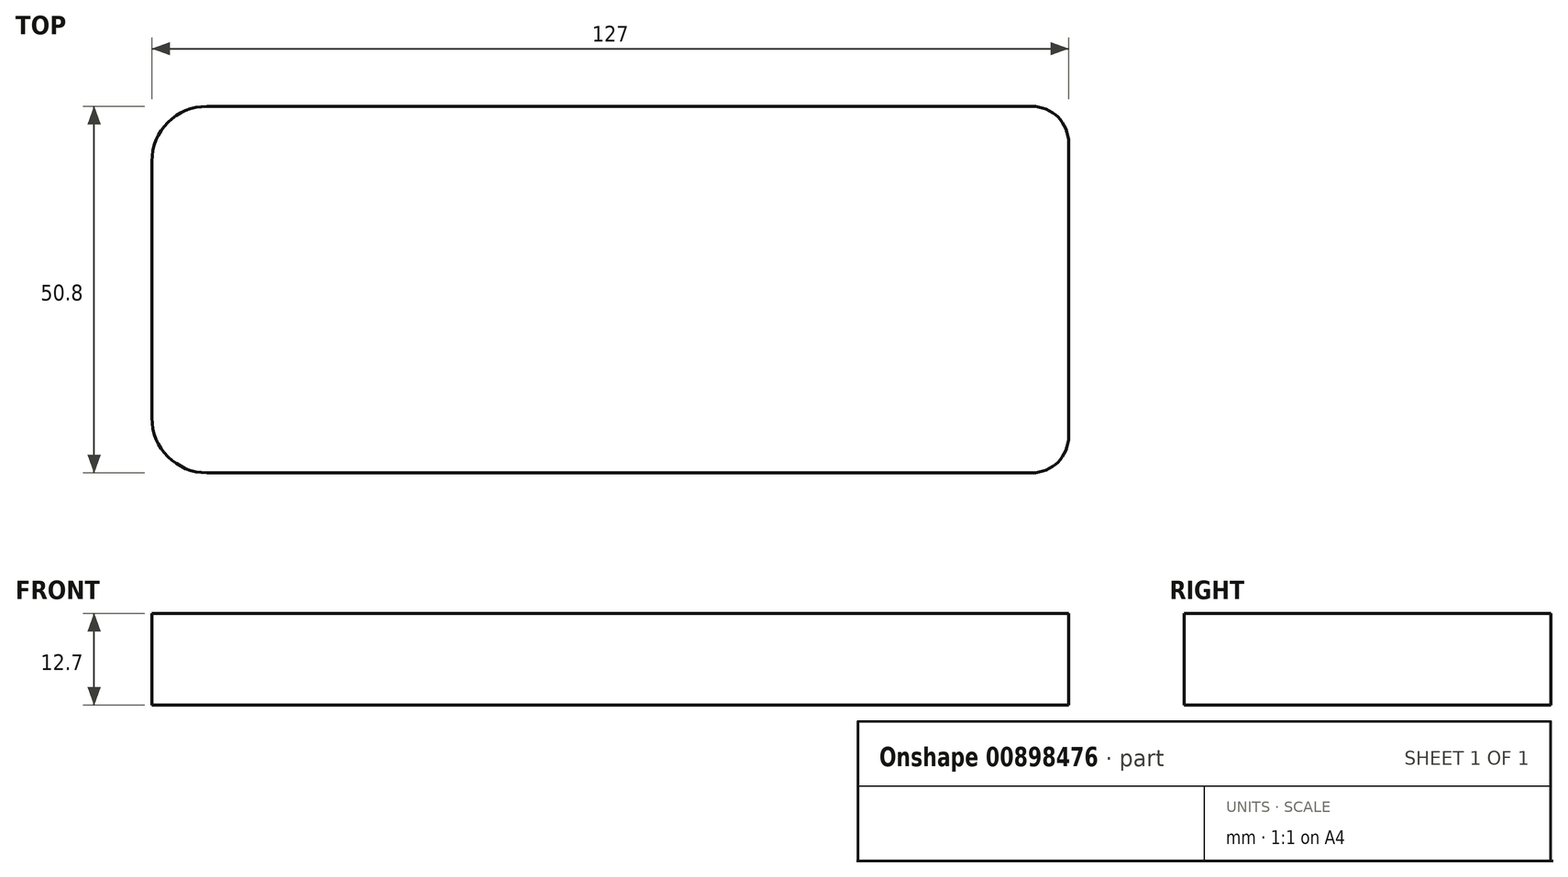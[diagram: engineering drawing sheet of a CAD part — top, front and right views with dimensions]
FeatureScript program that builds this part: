
annotation { "Feature Type Name" : "Feature", "Feature Type Description" : "" }
export const myFeature = defineFeature(function(context is Context, id is Id, definition is map)
    precondition{}
    {
        {
            var Q0;
            Q0=qCreatedBy(makeId("Top.planeOp"),FACE);
            var sketch = newSketch(context, id + "F0", { "sketchPlane" : qUnion([Q0])});
            skLineSegment(sketch, "E0", {"start": v(0, 0) * mm, "end": v(60.96, 0) * mm, "construction": true});
            skLineSegment(sketch, "E1", {"start": v(0, 0) * mm, "end": v(-66.04, 0) * mm, "construction": true});
            skPoint(sketch, "E2", {"position": v(30.48, 0) * mm});
            skLineSegment(sketch, "E3", {"start": v(30.48, 0) * mm, "end": v(30.48, -25.4) * mm, "construction": true});
            skLineSegment(sketch, "E4", {"start": v(30.48, 0) * mm, "end": v(30.48, 25.4) * mm, "construction": true});
            skLineSegment(sketch, "E5", {"start": v(30.48, 25.4) * mm, "end": v(50.8, 25.4) * mm});
            skLineSegment(sketch, "E6", {"start": v(60.96, 0) * mm, "end": v(60.96, 15.24) * mm});
            skLineSegment(sketch, "E7.MirrorCS", {"start": v(30.48, -25.4) * mm, "end": v(50.8, -25.4) * mm});
            skLineSegment(sketch, "E8.MirrorCS", {"start": v(60.96, 0) * mm, "end": v(60.96, -15.24) * mm});
            skLineSegment(sketch, "E9", {"start": v(-66.04, 0) * mm, "end": v(-66.04, 17.78) * mm});
            skLineSegment(sketch, "E10", {"start": v(-66.04, 0) * mm, "end": v(-66.04, -17.78) * mm});
            skLineSegment(sketch, "E11", {"start": v(30.48, -25.4) * mm, "end": v(-58.42, -25.4) * mm});
            skLineSegment(sketch, "E12", {"start": v(30.48, 25.4) * mm, "end": v(-58.42, 25.4) * mm});
            skArc(sketch, "E13.filletArc", {"start": v(-66.04, -17.78) * mm, "mid": v(-63.8, -23.17) * mm, "end": v(-58.42, -25.4) * mm});
            skArc(sketch, "E14.filletArc", {"start": v(-58.42, 25.4) * mm, "mid": v(-63.8, 23.17) * mm, "end": v(-66.04, 17.78) * mm});
            skLineSegment(sketch, "E15", {"start": v(50.8, -25.4) * mm, "end": v(55.88, -25.4) * mm});
            skLineSegment(sketch, "E16", {"start": v(50.8, 25.4) * mm, "end": v(55.88, 25.4) * mm});
            skLineSegment(sketch, "E17", {"start": v(60.96, 15.24) * mm, "end": v(60.96, 20.32) * mm});
            skLineSegment(sketch, "E18", {"start": v(60.96, -15.24) * mm, "end": v(60.96, -20.32) * mm});
            skPoint(sketch, "E19.newPointB", {"position": v(60.96, -25.4) * mm});
            skArc(sketch, "E19.filletArc", {"start": v(55.88, -25.4) * mm, "mid": v(59.47, -23.91) * mm, "end": v(60.96, -20.32) * mm});
            skPoint(sketch, "E20.newPointB", {"position": v(60.96, 25.4) * mm});
            skArc(sketch, "E20.filletArc", {"start": v(60.96, 20.32) * mm, "mid": v(59.47, 23.91) * mm, "end": v(55.88, 25.4) * mm});
            skSolve(sketch);
        }
        {
            var Q0;
            Q0 = qConstructionFilter(qBodyType(qCreatedBy(id + "F0" ,EDGE), BodyType.WIRE), ConstructionObject.NO);
            extrude(context, id + "F1", {"bodyType" : ToolBodyType.SURFACE, "surfaceEntities" : qUnion([Q0]), "depth" : 12.7 * mm, "offsetDistance" : 25.4 * mm});
        }
    });
